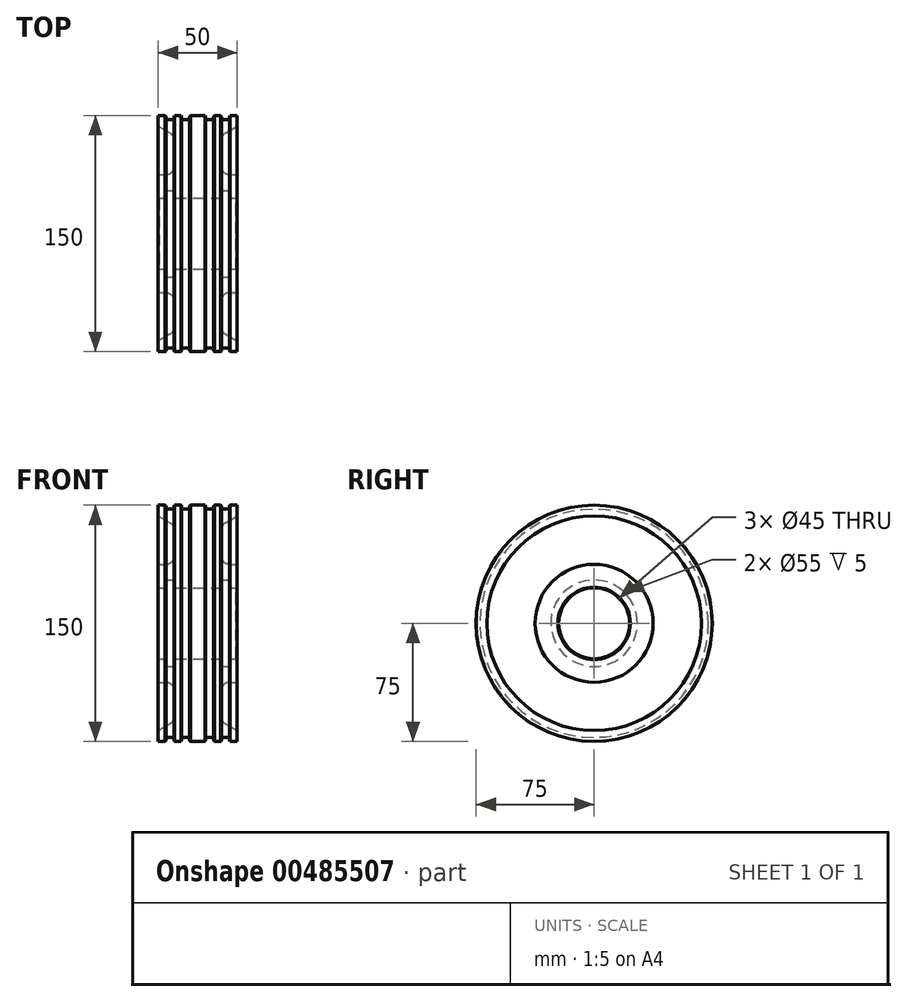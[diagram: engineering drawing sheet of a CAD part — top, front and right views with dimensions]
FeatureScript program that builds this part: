
annotation { "Feature Type Name" : "Feature", "Feature Type Description" : "" }
export const myFeature = defineFeature(function(context is Context, id is Id, definition is map)
    precondition{}
    {
        {
            var Q0;
            Q0=qCreatedBy(makeId("Front.planeOp"),FACE);
            var sketch = newSketch(context, id + "F0", { "sketchPlane" : qUnion([Q0])});
            skLineSegment(sketch, "E0", {"start": v(0, 0) * mm, "end": v(-116.65, 0) * mm, "construction": true});
            skLineSegment(sketch, "E1", {"start": v(0, 0) * mm, "end": v(0, 54.64) * mm, "construction": true});
            skLineSegment(sketch, "E2.top", {"start": v(0, 75) * mm, "end": v(-5.13, 75) * mm});
            skLineSegment(sketch, "E2.right", {"start": v(-25, 22.5) * mm, "end": v(-25, 37.5) * mm});
            skLineSegment(sketch, "E3", {"start": v(-25, 68.16) * mm, "end": v(-17.57, 63.87) * mm});
            skLineSegment(sketch, "E4", {"start": v(-15.07, 59.54) * mm, "end": v(-15.07, 42.5) * mm});
            skLineSegment(sketch, "E5", {"start": v(-20.07, 37.5) * mm, "end": v(-25, 37.5) * mm});
            skLineSegment(sketch, "E6", {"start": v(-25, 22.5) * mm, "end": v(-20, 22.5) * mm});
            skLineSegment(sketch, "E7.trimOffspring", {"start": v(-25, 68.16) * mm, "end": v(-25, 75) * mm});
            skPoint(sketch, "E8.visualSharp", {"position": v(-15.07, 37.5) * mm});
            skArc(sketch, "E8.filletArc", {"start": v(-20.07, 37.5) * mm, "mid": v(-16.53, 38.96) * mm, "end": v(-15.07, 42.5) * mm});
            skPoint(sketch, "E9.visualSharp", {"position": v(-15.07, 62.42) * mm});
            skArc(sketch, "E9.filletArc", {"start": v(-15.07, 59.54) * mm, "mid": v(-15.74, 62.04) * mm, "end": v(-17.57, 63.87) * mm});
            skLineSegment(sketch, "E10", {"start": v(-20, 22.5) * mm, "end": v(-20, 27.5) * mm});
            skLineSegment(sketch, "E11", {"start": v(-20, 27.5) * mm, "end": v(-15, 27.5) * mm});
            skLineSegment(sketch, "E12", {"start": v(-15, 27.5) * mm, "end": v(-15, 22.5) * mm});
            skLineSegment(sketch, "E13.trimOffspring", {"start": v(-15, 22.5) * mm, "end": v(0, 22.5) * mm});
            skLineSegment(sketch, "E14", {"start": v(-20.13, 75) * mm, "end": v(-20.13, 72.5) * mm});
            skLineSegment(sketch, "E15", {"start": v(-20.13, 72.5) * mm, "end": v(-15.13, 72.5) * mm});
            skLineSegment(sketch, "E16", {"start": v(-15.13, 72.5) * mm, "end": v(-15.13, 75) * mm});
            skLineSegment(sketch, "E17.1.0.0", {"start": v(-10.13, 72.5) * mm, "end": v(-5.13, 72.5) * mm});
            skLineSegment(sketch, "E17.1.0.1", {"start": v(-10.13, 75) * mm, "end": v(-10.13, 72.5) * mm});
            skLineSegment(sketch, "E17.1.0.2", {"start": v(-5.13, 72.5) * mm, "end": v(-5.13, 75) * mm});
            skLineSegment(sketch, "E17.direction1", {"start": v(-20.13, 72.5) * mm, "end": v(-15.13, 72.5) * mm, "construction": true});
            skLineSegment(sketch, "E18.trimOffspring", {"start": v(-20.13, 75) * mm, "end": v(-25, 75) * mm});
            skLineSegment(sketch, "E19.trimOffspring", {"start": v(-10.13, 75) * mm, "end": v(-15.13, 75) * mm});
            skLineSegment(sketch, "E20.MirrorCS", {"start": v(10.13, 75) * mm, "end": v(10.13, 72.5) * mm});
            skLineSegment(sketch, "E21.MirrorCS", {"start": v(20.13, 75) * mm, "end": v(20.13, 72.5) * mm});
            skLineSegment(sketch, "E22.MirrorCS", {"start": v(20.13, 72.5) * mm, "end": v(15.13, 72.5) * mm});
            skLineSegment(sketch, "E23.MirrorCS", {"start": v(20.13, 75) * mm, "end": v(25, 75) * mm});
            skLineSegment(sketch, "E24.MirrorCS", {"start": v(10.13, 72.5) * mm, "end": v(5.13, 72.5) * mm});
            skLineSegment(sketch, "E25.MirrorCS", {"start": v(20.13, 72.5) * mm, "end": v(15.13, 72.5) * mm, "construction": true});
            skLineSegment(sketch, "E26.MirrorCS", {"start": v(10.13, 75) * mm, "end": v(15.13, 75) * mm});
            skLineSegment(sketch, "E27.MirrorCS", {"start": v(15.13, 72.5) * mm, "end": v(15.13, 75) * mm});
            skLineSegment(sketch, "E28.MirrorCS", {"start": v(15, 27.5) * mm, "end": v(15, 22.5) * mm});
            skLineSegment(sketch, "E29.MirrorCS", {"start": v(0, 75) * mm, "end": v(5.13, 75) * mm});
            skLineSegment(sketch, "E30.MirrorCS", {"start": v(25, 68.16) * mm, "end": v(17.57, 63.87) * mm});
            skLineSegment(sketch, "E31.MirrorCS", {"start": v(25, 22.5) * mm, "end": v(20, 22.5) * mm});
            skArc(sketch, "E32.MirrorCS", {"start": v(15.07, 59.54) * mm, "mid": v(15.74, 62.04) * mm, "end": v(17.57, 63.87) * mm});
            skLineSegment(sketch, "E33.MirrorCS", {"start": v(20, 22.5) * mm, "end": v(20, 27.5) * mm});
            skLineSegment(sketch, "E34.MirrorCS", {"start": v(20, 27.5) * mm, "end": v(15, 27.5) * mm});
            skLineSegment(sketch, "E35.MirrorCS", {"start": v(5.13, 72.5) * mm, "end": v(5.13, 75) * mm});
            skLineSegment(sketch, "E36.MirrorCS", {"start": v(25, 22.5) * mm, "end": v(25, 37.5) * mm});
            skLineSegment(sketch, "E37.MirrorCS", {"start": v(20.07, 37.5) * mm, "end": v(25, 37.5) * mm});
            skLineSegment(sketch, "E38.MirrorCS", {"start": v(25, 68.16) * mm, "end": v(25, 75) * mm});
            skArc(sketch, "E39.MirrorCS", {"start": v(20.07, 37.5) * mm, "mid": v(16.53, 38.96) * mm, "end": v(15.07, 42.5) * mm});
            skLineSegment(sketch, "E40.MirrorCS", {"start": v(15, 22.5) * mm, "end": v(0, 22.5) * mm});
            skLineSegment(sketch, "E41.MirrorCS", {"start": v(15.07, 59.54) * mm, "end": v(15.07, 42.5) * mm});
            skPoint(sketch, "E42.MirrorP", {"position": v(15.07, 37.5) * mm});
            skPoint(sketch, "E43.MirrorP", {"position": v(15.07, 62.42) * mm});
            skSolve(sketch);
        }
        {
            var Q0;
            Q0 = qSketchRegion(id + "F0", true);
            var Q1;
            Q1=sQuery(id+"F0.wireOp",EDGE,"E0");
            revolve(context, id + "F1", {"entities" : qUnion([Q0]), "axis" : qUnion([Q1]), "revolveType" : RevolveType.FULL});
        }
        {
            var Q0;
            Q0=makeQuery(id+"F1.opRevolve","SWEPT_EDGE",EDGE,{"disambiguationData":[OSD([sQuery(id+"F0.wireOp",EDGE,"E12"),sQuery(id+"F0.wireOp",EDGE,"E13.trimOffspring")])]});
            var Q1;
            Q1=makeQuery(id+"F1.opRevolve","SWEPT_EDGE",EDGE,{"disambiguationData":[OSD([sQuery(id+"F0.wireOp",EDGE,"E31.MirrorCS"),sQuery(id+"F0.wireOp",EDGE,"E33.MirrorCS")])]});
            var Q2;
            Q2=makeQuery(id+"F1.opRevolve","SWEPT_EDGE",EDGE,{"disambiguationData":[OSD([sQuery(id+"F0.wireOp",EDGE,"E28.MirrorCS"),sQuery(id+"F0.wireOp",EDGE,"E40.MirrorCS")])]});
            var Q3;
            Q3=makeQuery(id+"F1.opRevolve","SWEPT_EDGE",EDGE,{"disambiguationData":[OSD([sQuery(id+"F0.wireOp",EDGE,"E6"),sQuery(id+"F0.wireOp",EDGE,"E10")])]});
            var Q4;
            Q4=makeQuery(id+"F1.opRevolve","SWEPT_EDGE",EDGE,{"disambiguationData":[OSD([sQuery(id+"F0.wireOp",EDGE,"E2.right"),sQuery(id+"F0.wireOp",EDGE,"E6")])]});
            var Q5;
            Q5=makeQuery(id+"F1.opRevolve","SWEPT_EDGE",EDGE,{"disambiguationData":[OSD([sQuery(id+"F0.wireOp",EDGE,"E31.MirrorCS"),sQuery(id+"F0.wireOp",EDGE,"E36.MirrorCS")])]});
            var Q6;
            Q6=makeQuery(id+"F1.opRevolve","SWEPT_EDGE",EDGE,{"disambiguationData":[OSD([sQuery(id+"F0.wireOp",EDGE,"E26.MirrorCS"),sQuery(id+"F0.wireOp",EDGE,"E27.MirrorCS")])]});
            var Q7;
            Q7=makeQuery(id+"F1.opRevolve","SWEPT_EDGE",EDGE,{"disambiguationData":[OSD([sQuery(id+"F0.wireOp",EDGE,"E29.MirrorCS"),sQuery(id+"F0.wireOp",EDGE,"E35.MirrorCS")])]});
            var Q8;
            Q8=makeQuery(id+"F1.opRevolve","SWEPT_EDGE",EDGE,{"disambiguationData":[OSD([sQuery(id+"F0.wireOp",EDGE,"E17.1.0.1"),sQuery(id+"F0.wireOp",EDGE,"E19.trimOffspring")])]});
            var Q9;
            Q9=makeQuery(id+"F1.opRevolve","SWEPT_EDGE",EDGE,{"disambiguationData":[OSD([sQuery(id+"F0.wireOp",EDGE,"E14"),sQuery(id+"F0.wireOp",EDGE,"E18.trimOffspring")])]});
            var Q10;
            Q10=makeQuery(id+"F1.opRevolve","SWEPT_EDGE",EDGE,{"disambiguationData":[OSD([sQuery(id+"F0.wireOp",EDGE,"E16"),sQuery(id+"F0.wireOp",EDGE,"E19.trimOffspring")])]});
            var Q11;
            Q11=makeQuery(id+"F1.opRevolve","SWEPT_EDGE",EDGE,{"disambiguationData":[OSD([sQuery(id+"F0.wireOp",EDGE,"E2.top"),sQuery(id+"F0.wireOp",EDGE,"E17.1.0.2")])]});
            var Q12;
            Q12=makeQuery(id+"F1.opRevolve","SWEPT_EDGE",EDGE,{"disambiguationData":[OSD([sQuery(id+"F0.wireOp",EDGE,"E20.MirrorCS"),sQuery(id+"F0.wireOp",EDGE,"E26.MirrorCS")])]});
            var Q13;
            Q13=makeQuery(id+"F1.opRevolve","SWEPT_EDGE",EDGE,{"disambiguationData":[OSD([sQuery(id+"F0.wireOp",EDGE,"E21.MirrorCS"),sQuery(id+"F0.wireOp",EDGE,"E23.MirrorCS")])]});
            chamfer(context, id + "F2", {"entities" : qUnion([Q0, Q1, Q2, Q3, Q4, Q5, Q6, Q7, Q8, Q9, Q10, Q11, Q12, Q13]), "width" : .5 * mm, "tangentPropagation" : true});
        }
    });
